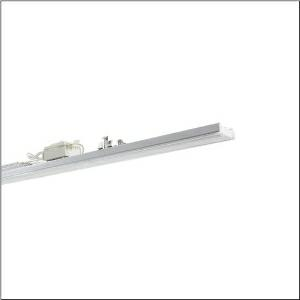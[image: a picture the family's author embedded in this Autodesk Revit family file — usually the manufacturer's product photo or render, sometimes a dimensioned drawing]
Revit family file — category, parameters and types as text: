
# Revit family: licross_21_recessed_ho_52tl18cn4c5m
name_source: partatom
category: Lighting Fixtures
units: mm (PartAtom-declared; Revit-internal decimal feet)

## family parameters
Cut with Voids When Loaded = No
Host = Face
Light Source = No
Part Type = Normal
Room Calculation Point = No
Round Connector Dimension = Use Diameter
Shared = No

## types (1)
- --- (1 x LED, 12540 lm, 68.4 W, 4000K)
    Apparent Load = 68 VA
    CIE Flux Codes = 75 94 99 100 100
    Color Rendering = 80
    Color Temperature = 4000K
    Default Elevation = 1800 mm
    Description = Licross 21 Recessed HO, luminaire insert, of sheet steel, galvanised, coil coated, white, length: 1.500mm, width: 66mm, height: 67mm, LED rated luminous flux: 12.540lm, light colour: 840, SDCM (Standard Deviation of Colour Matching)MacAdam ≤ 3 SDCM (initial), control gear: ON/OFF Multilumen, CLOi, with plug, 3-pole, with phase selection, mains connection: 220..240V, AC, 50/60Hz, internal wiring halogen-free, primary light control with lens, of plastic, primary optical cover: cover, of PMMA, light emission: direct distribution, primary light characteristic: symmetric, protection rating (complete): IP40, insulation class (complete): insulation class I (protective earthing), certification: CE, ENEC, VDE, UKCA, protection symbol: D if used in an environment without relevant dust loads with corresponding accessories, impact resistance: IK06, permissible ambient temperature for indoor applications: -35..+30°C, corresponds to IFS (International Featured Standards) requirements for safety and quality in the food industry, reducing of maximum allowable ambient temperature of 5°C with ceiling mounting, LABS conformity tested according to VDMA 24364:2018-05, The light source and the operating device comply with the requirements of the Ecodesign Regulation (EU) 2019/2020 and are replaceable in accordance with this regulation, packaging unit: 1 piece
    Height = 58 mm
    Lamp = 1 x LED
    Lamp Light Flux = 12540 lm
    Lamp Power = 68.4 W
    Lamp count = 1
    Length = 1500 mm
    Luminous efficacy = 183 lm/W
    Manufacturer = Siteco
    ModVariant = No
    Model = 52TL18CN4C5M
    Mounting Place = Ceiling
    Mounting Type = Pendant
    Number of Poles = 1
    OnlyDefault = Yes
    Power Factor = 1
    Product Name = Licross 21 Recessed HO
    Product group = luminaire insert | ceiling pendant
    ProductGroupID = 901
    Protection Class = Protection class I
    Protection Degree = IP 40
    RLX_Detail_Level = 1
    RLX_Emergency_Light_Flux = 0 lm
    RLX_Emergency_Type = 0
    RLX_Emergency_Type_DB = No
    RlxData = <blob elided: 22561 chars, md5=b2496d61>
    Socket = socket
    Standby Power = 0 W
    System Light Flux = 12540 lm
    System Power = 68 W
    Type Comments = factory setting: luminous flux: 100 % | (A | C | E) | 161 mA
    Type Image = l_1296930.jpg
    URL = http://relux.com
    VarID = @adj_109905
    Voltage = 0 V
    Weight = 0.00 kg
    Width = 66 mm

## geometry (parser evidence)
native form markers: Blend x4, Sweep x9
no freeform markers — native parametric forms only
